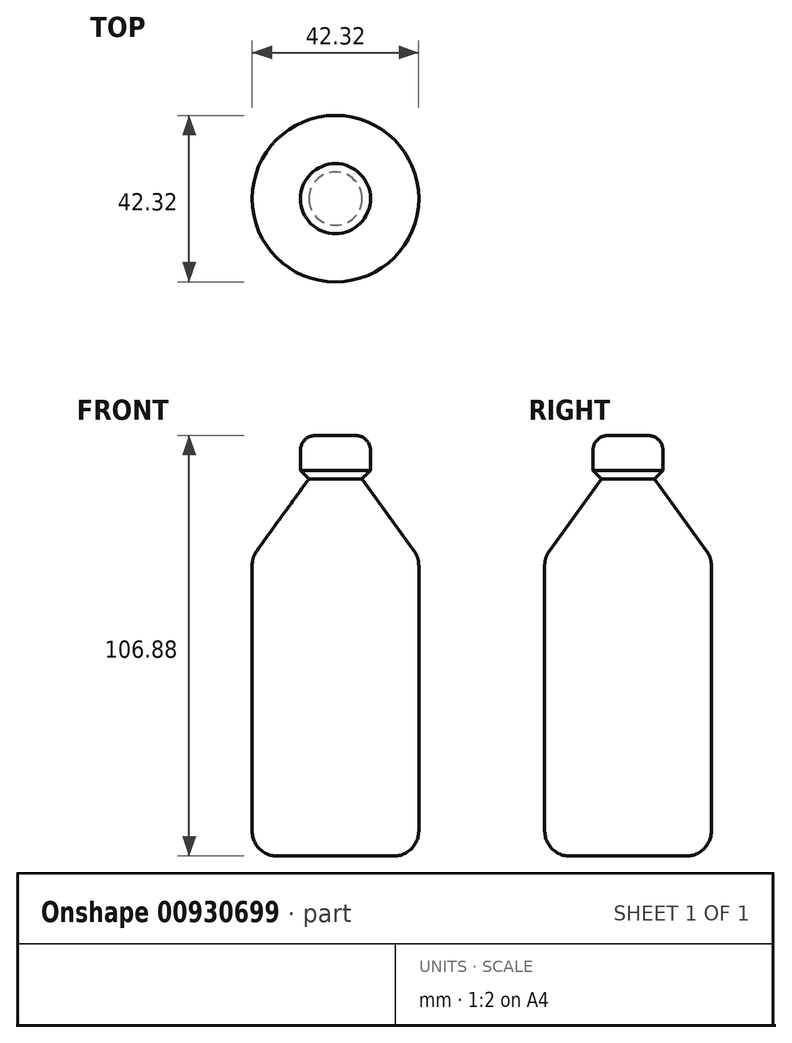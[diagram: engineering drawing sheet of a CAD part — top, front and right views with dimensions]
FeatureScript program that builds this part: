
annotation { "Feature Type Name" : "Feature", "Feature Type Description" : "" }
export const myFeature = defineFeature(function(context is Context, id is Id, definition is map)
    precondition{}
    {
        {
            var Q0;
            Q0=qCreatedBy(makeId("Right.planeOp"),FACE);
            var sketch = newSketch(context, id + "F0", { "sketchPlane" : qUnion([Q0])});
            skLineSegment(sketch, "E0.bottom", {"start": v(14.81, -46.47) * mm, "end": v(0, -46.47) * mm});
            skLineSegment(sketch, "E0.top", {"start": v(8.86, 46.47) * mm, "end": v(0, 46.47) * mm});
            skLineSegment(sketch, "E0.left", {"start": v(21.16, -40.12) * mm, "end": v(21.16, 27.4) * mm});
            skPoint(sketch, "E0.middle", {"position": v(0, 0) * mm});
            skLineSegment(sketch, "E1", {"start": v(8.86, 46.47) * mm, "end": v(19.96, 31.12) * mm});
            skPoint(sketch, "E2.orphan", {"position": v(-21.16, 46.47) * mm});
            skPoint(sketch, "E3.orphan", {"position": v(21.16, 46.47) * mm});
            skPoint(sketch, "E4.visualSharp", {"position": v(-21.16, 29.46) * mm});
            skPoint(sketch, "E5.visualSharp", {"position": v(21.16, 29.46) * mm});
            skArc(sketch, "E5.filletArc", {"start": v(21.16, 27.4) * mm, "mid": v(20.85, 29.36) * mm, "end": v(19.96, 31.12) * mm});
            skPoint(sketch, "E6.visualSharp", {"position": v(-21.16, -46.47) * mm});
            skPoint(sketch, "E7.visualSharp", {"position": v(21.16, -46.47) * mm});
            skArc(sketch, "E7.filletArc", {"start": v(14.81, -46.47) * mm, "mid": v(19.3, -44.61) * mm, "end": v(21.16, -40.12) * mm});
            skLineSegment(sketch, "E8.bottom", {"start": v(0, 46.47) * mm, "end": v(8.9, 46.47) * mm});
            skLineSegment(sketch, "E8.top", {"start": v(0, 60.4) * mm, "end": v(5.1, 60.4) * mm});
            skLineSegment(sketch, "E8.right", {"start": v(8.9, 46.47) * mm, "end": v(8.9, 56.6) * mm});
            skPoint(sketch, "E9.visualSharp", {"position": v(-8.71, 60.4) * mm});
            skPoint(sketch, "E10.visualSharp", {"position": v(8.9, 60.4) * mm});
            skArc(sketch, "E10.filletArc", {"start": v(8.9, 56.6) * mm, "mid": v(7.79, 59.3) * mm, "end": v(5.1, 60.4) * mm});
            skLineSegment(sketch, "E11", {"start": v(0, 60.4) * mm, "end": v(0, -46.47) * mm});
            skPoint(sketch, "E12.orphan", {"position": v(-14.81, -46.47) * mm});
            skSolve(sketch);
        }
        {
            var Q0;
            {var subQ1=sQuery(id+"F0.wireOp",EDGE,"E0.bottom");Q0=makeQuery(id+"F0.imprint","IMPRINT",FACE,{"disambiguationData":[TD([[makeQuery(id+"F0.imprint","IMPRINT",EDGE,{"derivedFrom":subQ1}),-1.0]])]});}
            var Q1;
            {var subQ1=sQuery(id+"F0.wireOp",EDGE,"E8.top");Q1=makeQuery(id+"F0.imprint","IMPRINT",FACE,{"disambiguationData":[TD([[makeQuery(id+"F0.imprint","IMPRINT",EDGE,{"derivedFrom":subQ1}),-1.0]])]});}
            var Q2;
            Q2=sQuery(id+"F0.wireOp",EDGE,"E11");
            revolve(context, id + "F1", {"surfaceOperationType" : NewSurfaceOperationType.NEW, "entities" : qUnion([Q0, Q1]), "axis" : qUnion([Q2]), "revolveType" : RevolveType.FULL});
        }
        {
            var Q0;
            Q0=makeQuery(id+"F1.opRevolve","SWEPT_EDGE",EDGE,{"disambiguationData":[OSD([sQuery(id+"F0.wireOp",EDGE,"E8.bottom"),sQuery(id+"F0.wireOp",EDGE,"E8.right")])]});
            chamfer(context, id + "F2", {"entities" : qUnion([Q0]), "width" : 5.08 * mm, "tangentPropagation" : true});
        }
    });
